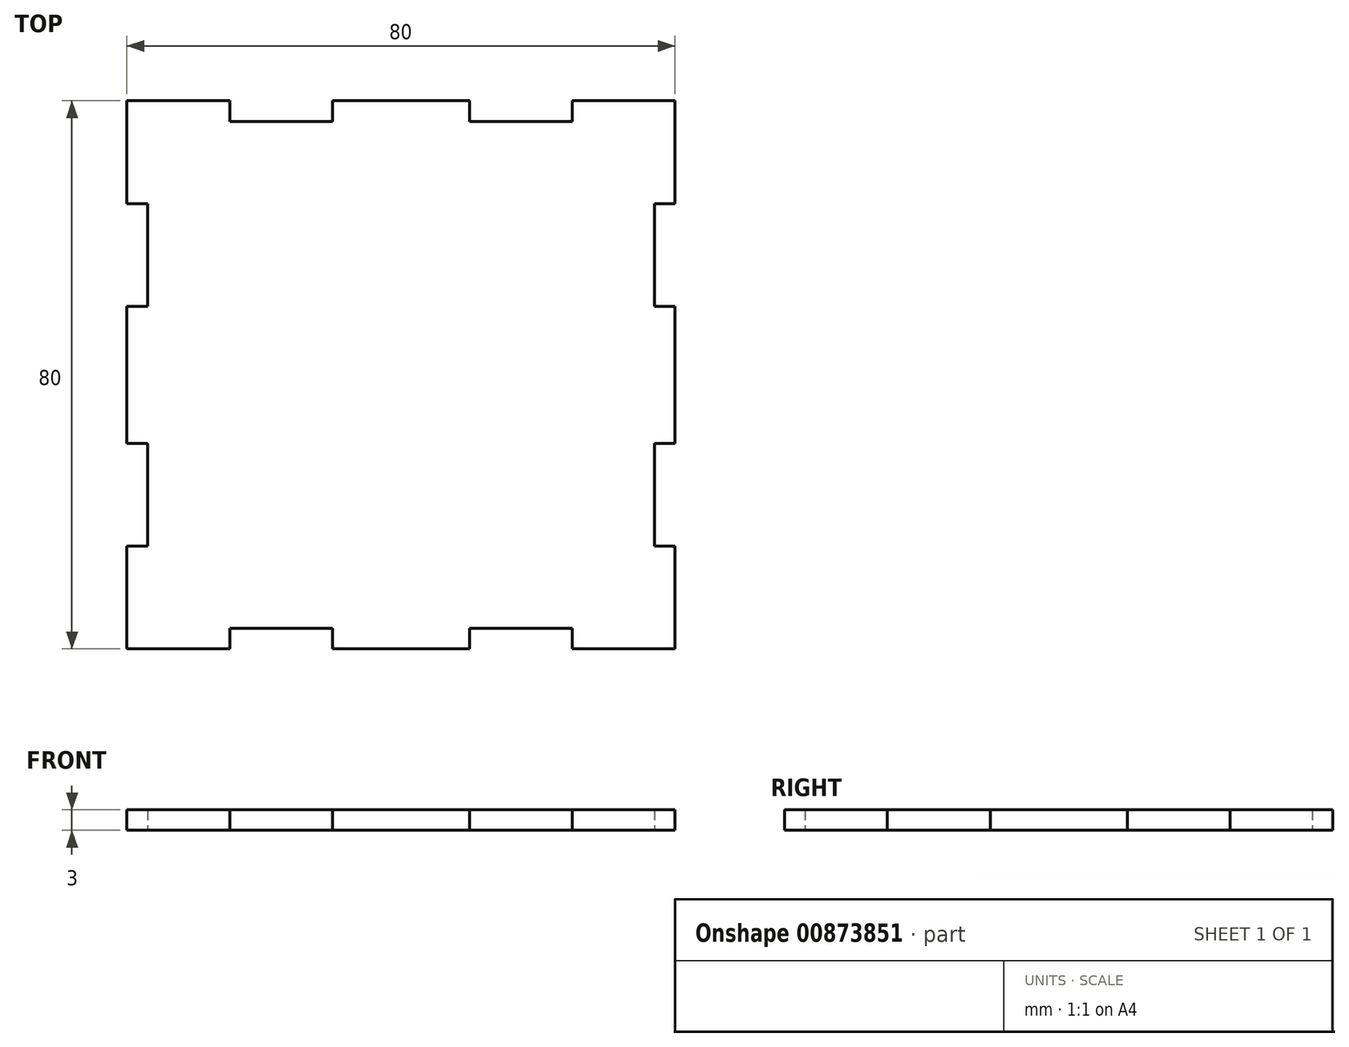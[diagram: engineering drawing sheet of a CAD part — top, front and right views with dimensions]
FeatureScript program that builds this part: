
annotation { "Feature Type Name" : "Feature", "Feature Type Description" : "" }
export const myFeature = defineFeature(function(context is Context, id is Id, definition is map)
    precondition{}
    {
        {
            var Q0;
            Q0=qCreatedBy(makeId("Top.planeOp"),FACE);
            var sketch = newSketch(context, id + "F0", { "sketchPlane" : qUnion([Q0])});
            skLineSegment(sketch, "E0.bottom", {"start": v(-40, 40) * mm, "end": v(-25, 40) * mm});
            skLineSegment(sketch, "E0.top", {"start": v(-40, -40) * mm, "end": v(-25, -40) * mm});
            skLineSegment(sketch, "E0.left", {"start": v(-40, 40) * mm, "end": v(-40, 25) * mm});
            skLineSegment(sketch, "E0.right", {"start": v(40, 40) * mm, "end": v(40, 25) * mm});
            skLineSegment(sketch, "E1", {"start": v(-25, 40) * mm, "end": v(-25, 37) * mm});
            skLineSegment(sketch, "E2", {"start": v(-25, 37) * mm, "end": v(-10, 37) * mm});
            skLineSegment(sketch, "E3", {"start": v(-10, 37) * mm, "end": v(-10, 40) * mm});
            skLineSegment(sketch, "E4.1.0.0", {"start": v(10, 37) * mm, "end": v(25, 37) * mm});
            skLineSegment(sketch, "E4.1.0.1", {"start": v(10, 40) * mm, "end": v(10, 37) * mm});
            skLineSegment(sketch, "E4.1.0.2", {"start": v(25, 37) * mm, "end": v(25, 40) * mm});
            skLineSegment(sketch, "E5.1.0", {"start": v(-37, -25) * mm, "end": v(-37, 10) * mm, "construction": true});
            skLineSegment(sketch, "E5.1.1", {"start": v(-37, 10) * mm, "end": v(-37, 25) * mm});
            skLineSegment(sketch, "E5.1.2", {"start": v(-37, 25) * mm, "end": v(-40, 25) * mm});
            skLineSegment(sketch, "E5.1.3", {"start": v(-37, -10) * mm, "end": v(-40, -10) * mm});
            skLineSegment(sketch, "E5.1.4", {"start": v(-40, -25) * mm, "end": v(-37, -25) * mm});
            skLineSegment(sketch, "E5.1.5", {"start": v(-37, -25) * mm, "end": v(-37, -10) * mm});
            skLineSegment(sketch, "E5.1.6", {"start": v(-40, 10) * mm, "end": v(-37, 10) * mm});
            skLineSegment(sketch, "E5.2.0", {"start": v(25, -37) * mm, "end": v(-10, -37) * mm, "construction": true});
            skLineSegment(sketch, "E5.2.1", {"start": v(-10, -37) * mm, "end": v(-25, -37) * mm});
            skLineSegment(sketch, "E5.2.2", {"start": v(-25, -37) * mm, "end": v(-25, -40) * mm});
            skLineSegment(sketch, "E5.2.3", {"start": v(10, -37) * mm, "end": v(10, -40) * mm});
            skLineSegment(sketch, "E5.2.4", {"start": v(25, -40) * mm, "end": v(25, -37) * mm});
            skLineSegment(sketch, "E5.2.5", {"start": v(25, -37) * mm, "end": v(10, -37) * mm});
            skLineSegment(sketch, "E5.2.6", {"start": v(-10, -40) * mm, "end": v(-10, -37) * mm});
            skLineSegment(sketch, "E5.3.0", {"start": v(37, 25) * mm, "end": v(37, -10) * mm, "construction": true});
            skLineSegment(sketch, "E5.3.1", {"start": v(37, -10) * mm, "end": v(37, -25) * mm});
            skLineSegment(sketch, "E5.3.2", {"start": v(37, -25) * mm, "end": v(40, -25) * mm});
            skLineSegment(sketch, "E5.3.3", {"start": v(37, 10) * mm, "end": v(40, 10) * mm});
            skLineSegment(sketch, "E5.3.4", {"start": v(40, 25) * mm, "end": v(37, 25) * mm});
            skLineSegment(sketch, "E5.3.5", {"start": v(37, 25) * mm, "end": v(37, 10) * mm});
            skLineSegment(sketch, "E5.3.6", {"start": v(40, -10) * mm, "end": v(37, -10) * mm});
            skPoint(sketch, "E5.center", {"position": v(0, 0) * mm});
            skLineSegment(sketch, "E6.trimOffspring", {"start": v(-10, 40) * mm, "end": v(10, 40) * mm});
            skLineSegment(sketch, "E7.trimOffspring", {"start": v(25, 40) * mm, "end": v(40, 40) * mm});
            skLineSegment(sketch, "E8.trimOffspring", {"start": v(40, 10) * mm, "end": v(40, -10) * mm});
            skLineSegment(sketch, "E9.trimOffspring", {"start": v(40, -25) * mm, "end": v(40, -40) * mm});
            skLineSegment(sketch, "E10.trimOffspring", {"start": v(-40, -25) * mm, "end": v(-40, -40) * mm});
            skLineSegment(sketch, "E11.trimOffspring", {"start": v(-40, 10) * mm, "end": v(-40, -10) * mm});
            skLineSegment(sketch, "E12.trimOffspring", {"start": v(-10, -40) * mm, "end": v(10, -40) * mm});
            skLineSegment(sketch, "E13.trimOffspring", {"start": v(25, -40) * mm, "end": v(40, -40) * mm});
            skSolve(sketch);
        }
        {
            var Q0;
            Q0 = qSketchRegion(id + "F0", true);
            extrude(context, id + "F1", {"entities" : qUnion([Q0]), "depth" : 3 * mm, "offsetDistance" : 25 * mm});
        }
    });
